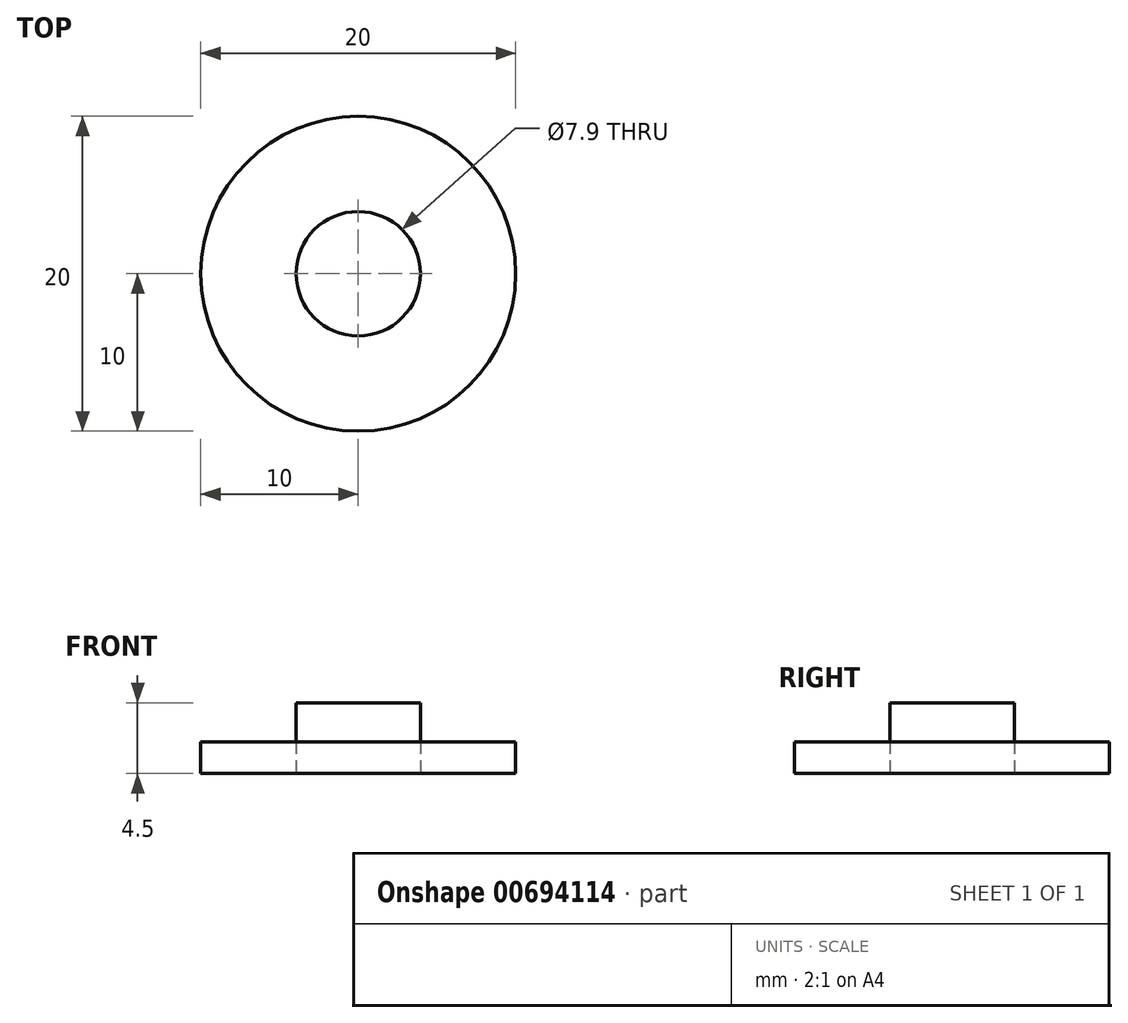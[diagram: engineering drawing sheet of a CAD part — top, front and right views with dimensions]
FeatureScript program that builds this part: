
annotation { "Feature Type Name" : "Feature", "Feature Type Description" : "" }
export const myFeature = defineFeature(function(context is Context, id is Id, definition is map)
    precondition{}
    {
        {
            var Q0;
            Q0=qCreatedBy(makeId("Front.planeOp"),FACE);
            var sketch = newSketch(context, id + "F0", { "sketchPlane" : qUnion([Q0])});
            skLineSegment(sketch, "E0.bottom", {"start": v(0, 0) * mm, "end": v(3.95, 0) * mm});
            skLineSegment(sketch, "E0.top", {"start": v(0, 4.5) * mm, "end": v(3.95, 4.5) * mm});
            skLineSegment(sketch, "E0.left", {"start": v(0, 0) * mm, "end": v(0, 4.5) * mm});
            skLineSegment(sketch, "E0.right", {"start": v(3.95, 0) * mm, "end": v(3.95, 4.5) * mm});
            skLineSegment(sketch, "E1.bottom", {"start": v(0, 0) * mm, "end": v(10, 0) * mm});
            skLineSegment(sketch, "E1.top", {"start": v(0, 2) * mm, "end": v(10, 2) * mm});
            skLineSegment(sketch, "E1.left", {"start": v(0, 0) * mm, "end": v(0, 2) * mm});
            skLineSegment(sketch, "E1.right", {"start": v(10, 0) * mm, "end": v(10, 2) * mm});
            skSolve(sketch);
        }
        {
            var Q0;
            {var subQ0=sQuery(id+"F0.wireOp",EDGE,"E0.top");Q0=makeQuery(id+"F0.imprint","IMPRINT",FACE,{"disambiguationData":[TD([[makeQuery(id+"F0.imprint","IMPRINT",EDGE,{"derivedFrom":subQ0}),-1.0]])]});}
            var Q1;
            {var subQ5=sQuery(id+"F0.wireOp",EDGE,"E1.left");Q1=makeQuery(id+"F0.imprint","IMPRINT",FACE,{"disambiguationData":[TD([[makeQuery(id+"F0.imprint","IMPRINT",EDGE,{"derivedFrom":subQ5}),-1.0]])]});}
            var Q2;
            {var subQ5=sQuery(id+"F0.wireOp",EDGE,"E1.right");Q2=makeQuery(id+"F0.imprint","IMPRINT",FACE,{"disambiguationData":[TD([[makeQuery(id+"F0.imprint","IMPRINT",EDGE,{"derivedFrom":subQ5}),1.0]])]});}
            var Q3;
            Q3=sQuery(id+"F0.wireOp",EDGE,"E0.left");
            revolve(context, id + "F1", {"entities" : qUnion([Q0, Q1, Q2]), "axis" : qUnion([Q3]), "revolveType" : RevolveType.FULL});
        }
    });
